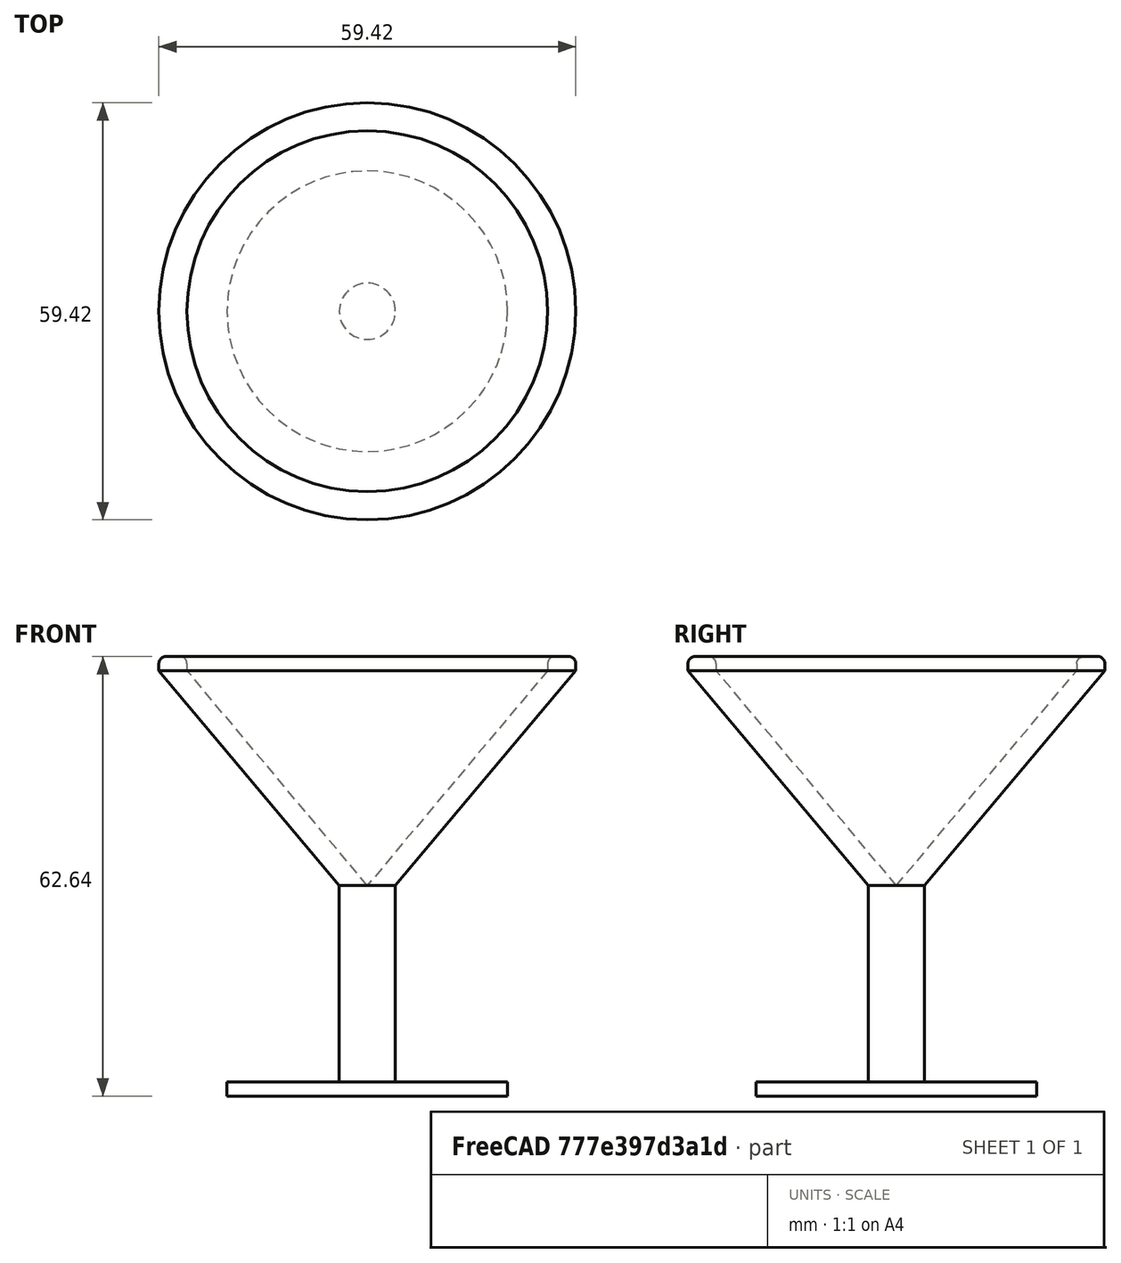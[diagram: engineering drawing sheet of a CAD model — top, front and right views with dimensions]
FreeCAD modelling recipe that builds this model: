
FCSTD DOCUMENT  (FreeCAD 0.18R16131 (Git))
Label: copa
License: All rights reserved
LicenseURL: http://en.wikipedia.org/wiki/All_rights_reserved
objects: Mesh::Feature×5, PartDesign::Fillet×4, Sketcher::SketchObject×1, PartDesign::Revolution×1, Spreadsheet::Sheet×1, PartDesign::Body×1
note: 8 computed .brp shape members not serialized (recipe doc carries the construction recipe); baked Part::Feature solids carry a one-line shape summary decoded from their .brp

FEATURE [Sketcher::SketchObject] Sketch
  MapMode = 5
  Placement = pos=(0,0,0) rot=(1,0,0;1.5708rad)
  Support = -> [XZ_Plane]
  expr: Constraints[21] = Spreadsheet.altura
  sketch-geometry (10):
    g0: LineSegment StartX=0 StartY=0 StartZ=0 EndX=20 EndY=0 EndZ=0
    g1: LineSegment StartX=20 StartY=0 StartZ=0 EndX=20 EndY=2 EndZ=0
    g2: LineSegment StartX=20 StartY=2 StartZ=0 EndX=4 EndY=2 EndZ=0
    g3: LineSegment StartX=4 StartY=2 StartZ=0 EndX=4 EndY=30 EndZ=0
    g4: LineSegment StartX=4 StartY=30 StartZ=0 EndX=29.7115 EndY=60.6418 EndZ=0
    g5: LineSegment StartX=29.7115 StartY=60.6418 StartZ=0 EndX=29.7115 EndY=62.6418 EndZ=0
    g6: LineSegment StartX=29.7115 StartY=62.6418 StartZ=0 EndX=25.7115 EndY=62.6418 EndZ=0
    g7: LineSegment StartX=25.7115 StartY=62.6418 StartZ=0 EndX=25.7115 EndY=60.6418 EndZ=0
    g8: LineSegment StartX=25.7115 StartY=60.6418 StartZ=0 EndX=0 EndY=30 EndZ=0
    g9: LineSegment StartX=0 StartY=30 StartZ=0 EndX=0 EndY=0 EndZ=0
  constraints (29):
    c: Coincident(g0,g1)
    c: Coincident(g1,g2)
    c: Coincident(g2,g3)
    c: Coincident(g3,g4)
    c: Coincident(g4,g5)
    c: Coincident(g5,g6)
    c: Coincident(g6,g7)
    c: Coincident(g7,g8)
    c: Coincident(g8,g9)
    c: Coincident(g9,g0)
    c: PointOnObject(g8,g-2)
    c: Vertical(g3)
    c: Vertical(g1)
    c: Vertical(g7)
    c: Vertical(g5)
    c: Horizontal(g2)
    c: Horizontal(g0)
    c: Horizontal(g6)
    c: Parallel(g8,g4)
    c: Horizontal(g8,g3)
    c: Coincident(g0,g-1)
    c: DistanceY(g9,g9) = 30
    c: DistanceX(g0,g0) = 20
    c: Distance(g4) = 40
    c: DistanceX(g8,g3) = 4
    c: Angle(g3,g4) = 2.44346
    c: DistanceY(g0,g1) = 2
    c: Equal(g5,g7)
    c: DistanceY(g5,g5) = 2
FEATURE [PartDesign::Revolution] Revolution
  Angle = 360
  Axis = (0,-2e-16,1)
  Base = (0,0,0)
  Placement = pos=(0,0,0) rot=(1,0,0;1.5708rad)
  Profile = -> Sketch
  ReferenceAxis = -> Sketch [V_Axis]
FEATURE [PartDesign::Fillet] Fillet
  Base = -> Revolution [Edge11,Edge9]
  BaseFeature = -> Revolution
  Placement = pos=(0,0,0) rot=(1,0,0;1.5708rad)
  Radius = 1
FEATURE [Spreadsheet::Sheet] Spreadsheet
  cells = A2=altura; B2(altura)=30
FEATURE [PartDesign::Fillet] Fillet001
  Base = -> Fillet [Edge6]
  BaseFeature = -> Fillet
  Placement = pos=(0,0,0) rot=(1,0,0;1.5708rad)
  Radius = 4
FEATURE [PartDesign::Fillet] Fillet002
  Base = -> Fillet001 [Edge9]
  BaseFeature = -> Fillet001
  Placement = pos=(0,0,0) rot=(1,0,0;1.5708rad)
  Radius = 14
FEATURE [Mesh::Feature] Mesh  label="Fillet002 (Meshed)"
FEATURE [Mesh::Feature] Mesh001  label="Fillet002 (Meshed)001"
FEATURE [Mesh::Feature] Mesh002  label="Body (Meshed)"
FEATURE [Mesh::Feature] Mesh003  label="Body (Meshed)001"
FEATURE [PartDesign::Fillet] Fillet003
  Base = -> Revolution [Edge9,Edge11]
  BaseFeature = -> Revolution
  Placement = pos=(0,0,0) rot=(1,0,0;1.5708rad)
  Radius = 1
FEATURE [PartDesign::Body] Body
  Group = -> [Sketch,Revolution,Fillet,Fillet001,Fillet002,Fillet003]
  Origin = -> Origin
  Tip = -> Fillet003
FEATURE [Mesh::Feature] Mesh004  label="Fillet003 (Meshed)"
